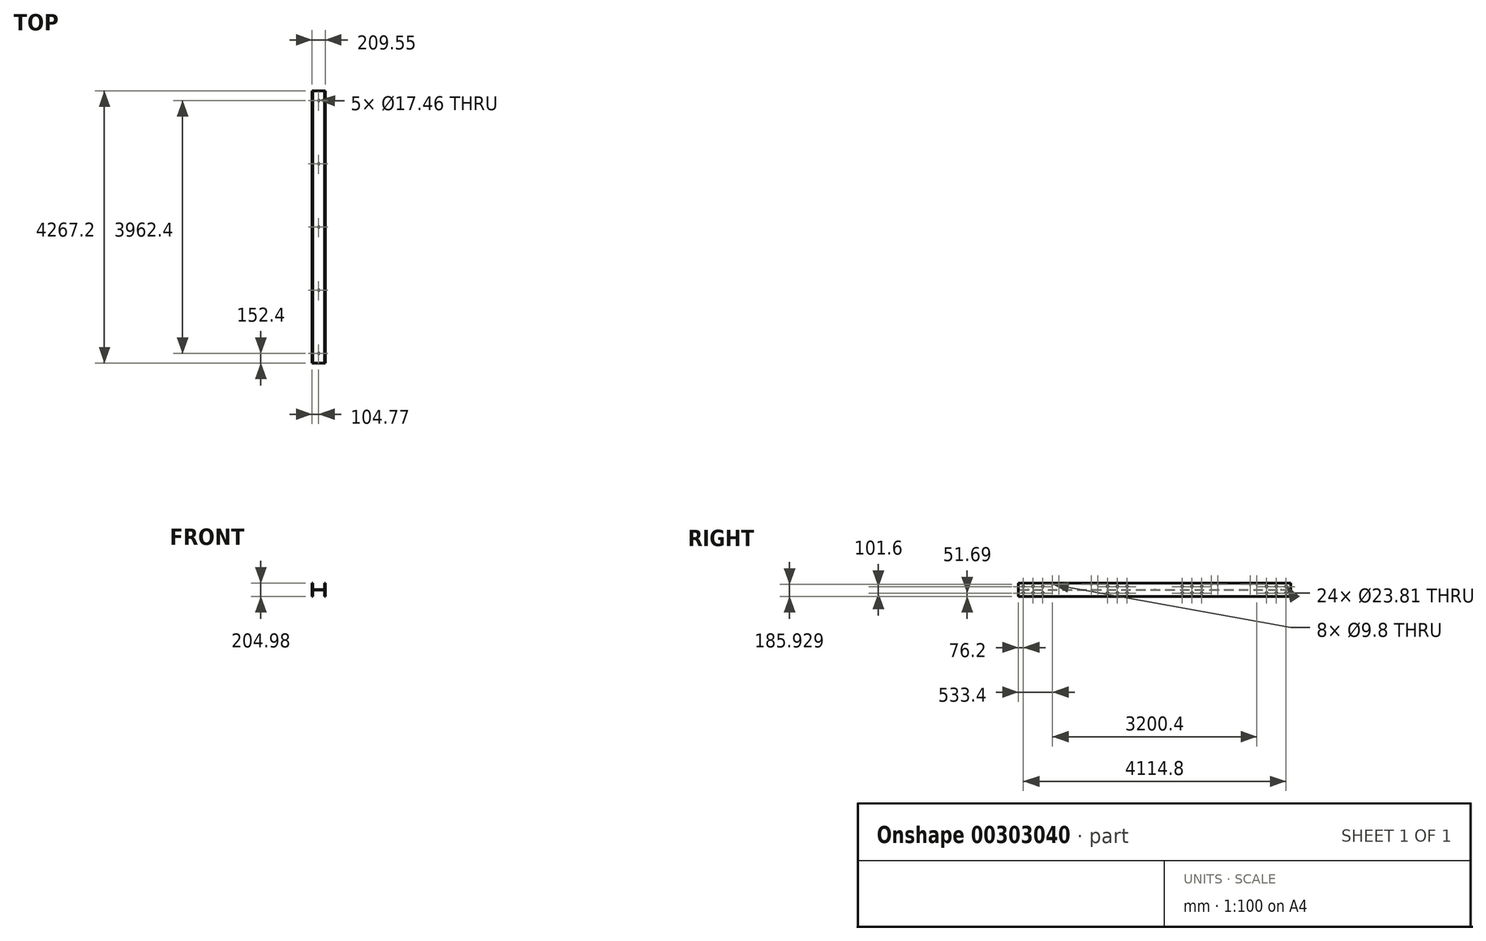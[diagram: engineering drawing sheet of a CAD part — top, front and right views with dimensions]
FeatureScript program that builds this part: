
annotation { "Feature Type Name" : "Feature", "Feature Type Description" : "" }
export const myFeature = defineFeature(function(context is Context, id is Id, definition is map)
    precondition{}
    {
        {
            var Q0;
            Q0=qCreatedBy(makeId("Front.planeOp"),FACE);
            var sketch = newSketch(context, id + "F0", { "sketchPlane" : qUnion([Q0])});
            skLineSegment(sketch, "E0", {"start": v(104.78, -102.49) * mm, "end": v(90.55, -102.49) * mm});
            skLineSegment(sketch, "E1", {"start": v(90.55, -102.49) * mm, "end": v(90.55, -22.1) * mm});
            skArc(sketch, "E2", {"start": v(90.55, -22.1) * mm, "mid": v(85.42, -9.7) * mm, "end": v(73.03, -4.57) * mm});
            skLineSegment(sketch, "E3", {"start": v(73.03, -4.57) * mm, "end": v(-73.03, -4.57) * mm});
            skArc(sketch, "E4", {"start": v(-73.03, -4.57) * mm, "mid": v(-85.42, -9.7) * mm, "end": v(-90.55, -22.1) * mm});
            skLineSegment(sketch, "E5", {"start": v(-90.55, -22.1) * mm, "end": v(-90.55, -102.49) * mm});
            skLineSegment(sketch, "E6", {"start": v(-90.55, -102.49) * mm, "end": v(-104.78, -102.49) * mm});
            skLineSegment(sketch, "E7", {"start": v(-104.78, -102.49) * mm, "end": v(-104.78, 102.49) * mm});
            skLineSegment(sketch, "E8", {"start": v(-104.78, 102.49) * mm, "end": v(-90.55, 102.49) * mm});
            skLineSegment(sketch, "E9", {"start": v(-90.55, 102.49) * mm, "end": v(-90.55, 22.1) * mm});
            skArc(sketch, "E10", {"start": v(-90.55, 22.1) * mm, "mid": v(-85.42, 9.7) * mm, "end": v(-73.03, 4.57) * mm});
            skLineSegment(sketch, "E11", {"start": v(-73.03, 4.57) * mm, "end": v(73.03, 4.57) * mm});
            skArc(sketch, "E12", {"start": v(73.03, 4.57) * mm, "mid": v(85.42, 9.7) * mm, "end": v(90.55, 22.1) * mm});
            skLineSegment(sketch, "E13", {"start": v(90.55, 22.1) * mm, "end": v(90.55, 102.49) * mm});
            skLineSegment(sketch, "E14", {"start": v(90.55, 102.49) * mm, "end": v(104.78, 102.49) * mm});
            skLineSegment(sketch, "E15", {"start": v(104.78, 102.49) * mm, "end": v(104.77, -102.49) * mm});
            skSolve(sketch);
        }
        {
            var Q0;
            Q0=makeQuery(id+"F0.imprint","IMPRINT",FACE,{"disambiguationData":[TD([[makeQuery(id+"F0.imprint","IMPRINT",EDGE,{"derivedFrom":sQuery(id+"F0.wireOp",EDGE,"E0")}),-1.0]])]});
            extrude(context, id + "F1", {"entities" : qUnion([Q0]), "depth" : 4267.2 * mm, "symmetric" : true});
        }
        {
            var Q0;
            Q0=qCreatedBy(makeId("Right.planeOp"),FACE);
            var sketch = newSketch(context, id + "F2", { "sketchPlane" : qUnion([Q0])});
            skLineSegment(sketch, "E16", {"start": v(-2295.65, 50.8) * mm, "end": v(2250.38, 50.8) * mm, "construction": true});
            skPoint(sketch, "E17", {"position": v(-2057.4, 50.8) * mm});
            skPoint(sketch, "E18", {"position": v(-1905, 50.8) * mm});
            skPoint(sketch, "E19", {"position": v(-1752.6, 50.8) * mm});
            skPoint(sketch, "E20", {"position": v(-736.6, 50.8) * mm});
            skPoint(sketch, "E21", {"position": v(-584.2, 50.8) * mm});
            skPoint(sketch, "E22", {"position": v(-431.8, 50.8) * mm});
            skPoint(sketch, "E23", {"position": v(431.8, 50.8) * mm});
            skPoint(sketch, "E24", {"position": v(584.2, 50.8) * mm});
            skPoint(sketch, "E25", {"position": v(736.6, 50.8) * mm});
            skPoint(sketch, "E26", {"position": v(1752.6, 50.8) * mm});
            skPoint(sketch, "E27", {"position": v(1905, 50.8) * mm});
            skPoint(sketch, "E28", {"position": v(2057.4, 50.8) * mm});
            skPoint(sketch, "E29", {"position": v(-2057.4, -50.8) * mm});
            skPoint(sketch, "E30", {"position": v(-1905, -50.8) * mm});
            skPoint(sketch, "E31", {"position": v(-1752.6, -50.8) * mm});
            skPoint(sketch, "E32", {"position": v(-736.6, -50.8) * mm});
            skPoint(sketch, "E33", {"position": v(-584.2, -50.8) * mm});
            skPoint(sketch, "E34", {"position": v(-431.8, -50.8) * mm});
            skPoint(sketch, "E35", {"position": v(431.8, -50.8) * mm});
            skPoint(sketch, "E36", {"position": v(584.2, -50.8) * mm});
            skPoint(sketch, "E37", {"position": v(736.6, -50.8) * mm});
            skPoint(sketch, "E38", {"position": v(1752.6, -50.8) * mm});
            skPoint(sketch, "E39", {"position": v(1905, -50.8) * mm});
            skPoint(sketch, "E40", {"position": v(2057.4, -50.8) * mm});
            skLineSegment(sketch, "E41", {"start": v(-2299.75, 83.44) * mm, "end": v(2245.38, 83.44) * mm, "construction": true});
            skPoint(sketch, "E42", {"position": v(-1600.2, 83.44) * mm});
            skPoint(sketch, "E43", {"position": v(-1498.6, 83.44) * mm});
            skPoint(sketch, "E44", {"position": v(-990.6, 83.44) * mm});
            skPoint(sketch, "E45", {"position": v(-889, 83.44) * mm});
            skLineSegment(sketch, "E46", {"start": v(-1244.6, 283.55) * mm, "end": v(-1244.6, -188.8) * mm, "construction": true});
            skPoint(sketch, "E47.0", {"position": v(0, 0) * mm});
            skLineSegment(sketch, "E48", {"start": v(0, 148.04) * mm, "end": v(0, -175.8) * mm, "construction": true});
            skPoint(sketch, "E49.MirrorP", {"position": v(889, 83.44) * mm});
            skPoint(sketch, "E50.MirrorP", {"position": v(990.6, 83.44) * mm});
            skPoint(sketch, "E51.MirrorP", {"position": v(1498.6, 83.44) * mm});
            skPoint(sketch, "E52.MirrorP", {"position": v(1600.2, 83.44) * mm});
            skSolve(sketch);
        }
        {
            var Q0;
            Q0=sQuery(id+"F2.wireOp",VERTEX,"E17");
            var Q1;
            Q1=sQuery(id+"F2.wireOp",VERTEX,"E18");
            var Q2;
            Q2=sQuery(id+"F2.wireOp",VERTEX,"E19");
            var Q3;
            Q3=sQuery(id+"F2.wireOp",VERTEX,"E29");
            var Q4;
            Q4=sQuery(id+"F2.wireOp",VERTEX,"E30");
            var Q5;
            Q5=sQuery(id+"F2.wireOp",VERTEX,"E31");
            var Q6;
            Q6=sQuery(id+"F2.wireOp",VERTEX,"E20");
            var Q7;
            Q7=sQuery(id+"F2.wireOp",VERTEX,"E21");
            var Q8;
            Q8=sQuery(id+"F2.wireOp",VERTEX,"E22");
            var Q9;
            Q9=sQuery(id+"F2.wireOp",VERTEX,"E32");
            var Q10;
            Q10=sQuery(id+"F2.wireOp",VERTEX,"E33");
            var Q11;
            Q11=sQuery(id+"F2.wireOp",VERTEX,"E34");
            var Q12;
            Q12=sQuery(id+"F2.wireOp",VERTEX,"E23");
            var Q13;
            Q13=sQuery(id+"F2.wireOp",VERTEX,"E24");
            var Q14;
            Q14=sQuery(id+"F2.wireOp",VERTEX,"E25");
            var Q15;
            Q15=sQuery(id+"F2.wireOp",VERTEX,"E35");
            var Q16;
            Q16=sQuery(id+"F2.wireOp",VERTEX,"E36");
            var Q17;
            Q17=sQuery(id+"F2.wireOp",VERTEX,"E37");
            var Q18;
            Q18=sQuery(id+"F2.wireOp",VERTEX,"E26");
            var Q19;
            Q19=sQuery(id+"F2.wireOp",VERTEX,"E27");
            var Q20;
            Q20=sQuery(id+"F2.wireOp",VERTEX,"E28");
            var Q21;
            Q21=sQuery(id+"F2.wireOp",VERTEX,"E38");
            var Q22;
            Q22=sQuery(id+"F2.wireOp",VERTEX,"E39");
            var Q23;
            Q23=sQuery(id+"F2.wireOp",VERTEX,"E40");
            var Q24;
            Q24=makeQuery(id+"F1.opExtrude","SWEPT_BODY",BODY,{"disambiguationData":[OSD([sQuery(id+"F0.wireOp",EDGE,"E0"),sQuery(id+"F0.wireOp",EDGE,"E1"),sQuery(id+"F0.wireOp",EDGE,"E2"),sQuery(id+"F0.wireOp",EDGE,"E3"),sQuery(id+"F0.wireOp",EDGE,"E4"),sQuery(id+"F0.wireOp",EDGE,"E5"),sQuery(id+"F0.wireOp",EDGE,"E6"),sQuery(id+"F0.wireOp",EDGE,"E7"),sQuery(id+"F0.wireOp",EDGE,"E8"),sQuery(id+"F0.wireOp",EDGE,"E9"),sQuery(id+"F0.wireOp",EDGE,"E10"),sQuery(id+"F0.wireOp",EDGE,"E11"),sQuery(id+"F0.wireOp",EDGE,"E12"),sQuery(id+"F0.wireOp",EDGE,"E13"),sQuery(id+"F0.wireOp",EDGE,"E14"),sQuery(id+"F0.wireOp",EDGE,"E15")])]});
            hole(context, id + "F3", {"style" : HoleStyle.SIMPLE, "endStyle" : HoleEndStyle.THROUGH, "oppositeDirection" : true, "holeDiameter" : 23.8 * mm, "tappedDepth" : 12.71 * mm, "tapClearance" : 3, "locations" : qUnion([Q0, Q1, Q2, Q3, Q4, Q5, Q6, Q7, Q8, Q9, Q10, Q11, Q12, Q13, Q14, Q15, Q16, Q17, Q18, Q19, Q20, Q21, Q22, Q23]), "scope" : qUnion([Q24])});
        }
        {
            var Q0;
            Q0=makeQuery(id+"F1.opExtrude","SWEPT_FACE",FACE,{"disambiguationData":[OSD([sQuery(id+"F0.wireOp",EDGE,"E11")])]});
            var sketch = newSketch(context, id + "F4", { "sketchPlane" : qUnion([Q0])});
            skLineSegment(sketch, "E53", {"start": v(0, 2464.15) * mm, "end": v(0, -2348.16) * mm, "construction": true});
            skPoint(sketch, "E54", {"position": v(0, 1981.2) * mm});
            skPoint(sketch, "E55", {"position": v(0, 990.6) * mm});
            skPoint(sketch, "E56", {"position": v(0, -990.6) * mm});
            skPoint(sketch, "E57", {"position": v(0, -1981.2) * mm});
            skPoint(sketch, "E58", {"position": v(0, 0) * mm});
            skSolve(sketch);
        }
        {
            var Q0;
            Q0=sQuery(id+"F4.wireOp",VERTEX,"E57");
            var Q1;
            Q1=sQuery(id+"F4.wireOp",VERTEX,"E56");
            var Q2;
            Q2=sQuery(id+"F4.wireOp",VERTEX,"E58");
            var Q3;
            Q3=sQuery(id+"F4.wireOp",VERTEX,"E55");
            var Q4;
            Q4=sQuery(id+"F4.wireOp",VERTEX,"E54");
            var Q5;
            Q5=makeQuery(id+"F1.opExtrude","SWEPT_BODY",BODY,{"disambiguationData":[OSD([sQuery(id+"F0.wireOp",EDGE,"E0"),sQuery(id+"F0.wireOp",EDGE,"E1"),sQuery(id+"F0.wireOp",EDGE,"E2"),sQuery(id+"F0.wireOp",EDGE,"E3"),sQuery(id+"F0.wireOp",EDGE,"E4"),sQuery(id+"F0.wireOp",EDGE,"E5"),sQuery(id+"F0.wireOp",EDGE,"E6"),sQuery(id+"F0.wireOp",EDGE,"E7"),sQuery(id+"F0.wireOp",EDGE,"E8"),sQuery(id+"F0.wireOp",EDGE,"E9"),sQuery(id+"F0.wireOp",EDGE,"E10"),sQuery(id+"F0.wireOp",EDGE,"E11"),sQuery(id+"F0.wireOp",EDGE,"E12"),sQuery(id+"F0.wireOp",EDGE,"E13"),sQuery(id+"F0.wireOp",EDGE,"E14"),sQuery(id+"F0.wireOp",EDGE,"E15")])]});
            hole(context, id + "F5", {"style" : HoleStyle.SIMPLE, "endStyle" : HoleEndStyle.THROUGH, "holeDiameter" : 17.46 * mm, "tappedDepth" : 12.7 * mm, "tapClearance" : 3, "locations" : qUnion([Q0, Q1, Q2, Q3, Q4]), "scope" : qUnion([Q5])});
        }
        {
            var Q0;
            Q0=sQuery(id+"F2.wireOp",VERTEX,"E42");
            var Q1;
            Q1=sQuery(id+"F2.wireOp",VERTEX,"E43");
            var Q2;
            Q2=sQuery(id+"F2.wireOp",VERTEX,"E44");
            var Q3;
            Q3=sQuery(id+"F2.wireOp",VERTEX,"E45");
            var Q4;
            Q4=sQuery(id+"F2.wireOp",VERTEX,"E49.MirrorP");
            var Q5;
            Q5=sQuery(id+"F2.wireOp",VERTEX,"E50.MirrorP");
            var Q6;
            Q6=sQuery(id+"F2.wireOp",VERTEX,"E51.MirrorP");
            var Q7;
            Q7=sQuery(id+"F2.wireOp",VERTEX,"E52.MirrorP");
            var Q8;
            Q8=makeQuery(id+"F1.opExtrude","SWEPT_BODY",BODY,{"disambiguationData":[OSD([sQuery(id+"F0.wireOp",EDGE,"E0"),sQuery(id+"F0.wireOp",EDGE,"E1"),sQuery(id+"F0.wireOp",EDGE,"E2"),sQuery(id+"F0.wireOp",EDGE,"E3"),sQuery(id+"F0.wireOp",EDGE,"E4"),sQuery(id+"F0.wireOp",EDGE,"E5"),sQuery(id+"F0.wireOp",EDGE,"E6"),sQuery(id+"F0.wireOp",EDGE,"E7"),sQuery(id+"F0.wireOp",EDGE,"E8"),sQuery(id+"F0.wireOp",EDGE,"E9"),sQuery(id+"F0.wireOp",EDGE,"E10"),sQuery(id+"F0.wireOp",EDGE,"E11"),sQuery(id+"F0.wireOp",EDGE,"E12"),sQuery(id+"F0.wireOp",EDGE,"E13"),sQuery(id+"F0.wireOp",EDGE,"E14"),sQuery(id+"F0.wireOp",EDGE,"E15")])]});
            hole(context, id + "F6", {"style" : HoleStyle.SIMPLE, "endStyle" : HoleEndStyle.THROUGH, "oppositeDirection" : true, "standardTappedOrClearance" : lookupTablePath({ "standard" : "ANSI", "fit" : "Close", "size" : "3/8", "type" : "Clearance" }), "standardBlindInLast" : lookupTablePath({ "fit" : "Close", "standard" : "ANSI", "size" : "3/8", "type" : "Clearance" }), "holeDiameter" : 9.8 * mm, "tappedDepth" : 12.7 * mm, "tapClearance" : 3, "locations" : qUnion([Q0, Q1, Q2, Q3, Q4, Q5, Q6, Q7]), "scope" : qUnion([Q8])});
        }
    });
